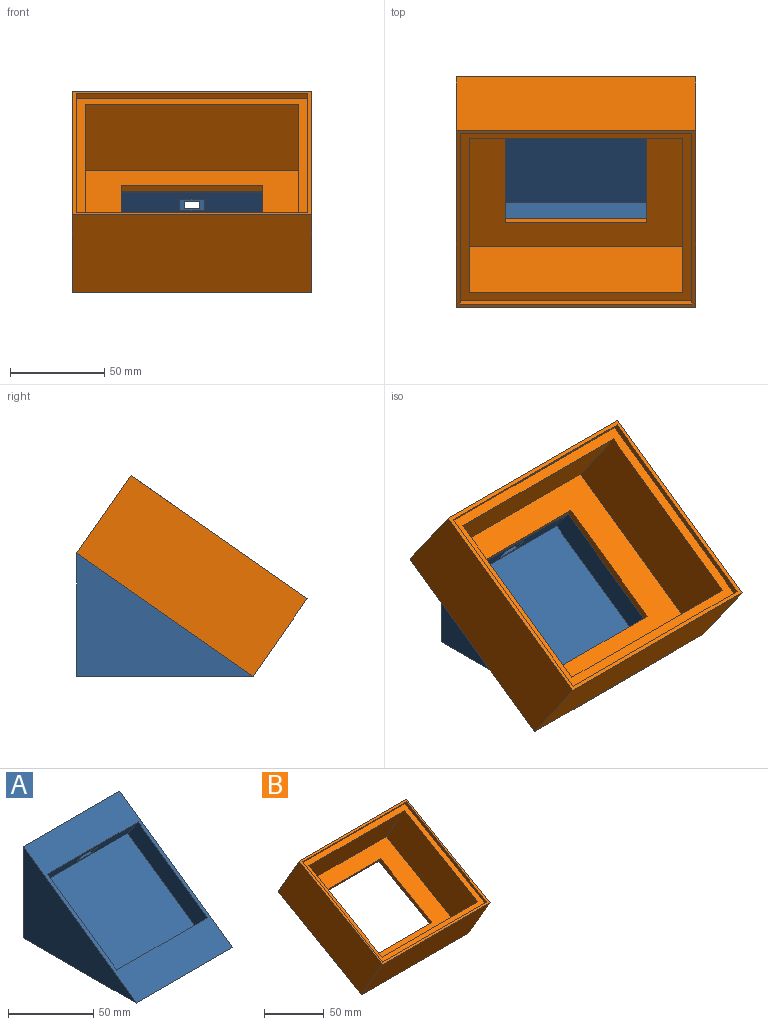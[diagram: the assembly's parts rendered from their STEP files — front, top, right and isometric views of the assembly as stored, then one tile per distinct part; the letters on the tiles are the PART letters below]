
ASSEMBLY  parts=2 mates=1
PART A: 33 faces, bbox 80x93.5x65.5 mm
  f0: plane 80x65.47mm, normal (0,1,0), area 5204.6mm2, adj f2,f3,f4,f5,f14,f15,f16,f17
  f1: plane 75x12.29mm, normal (0,-0.82,-0.57), area 1025.8mm2, adj f2,f6,f8,f9,f10,f11,f12,f13
  f2: plane 93.5x80mm, normal (0,-0.57,0.82), area 3881.4mm2, adj f0,f1,f3,f4,f5,f6,f7,f8
  f3: plane 93.5x80mm, normal (0,0,-1), area 1415.7mm2, adj f0,f2,f4,f5,f19,f20,f21,f22
  f4: plane 93.5x65.47mm, normal (1,0,0), area 3060.7mm2, adj f0,f2,f3
  f5: plane 93.5x65.47mm, normal (-1,0,0), area 3060.7mm2, adj f0,f2,f3
  f6: plane 65.94x52.44mm, normal (1,0,0), area 1050mm2, adj f1,f2,f7,f9
  f7: plane 75x12.29mm, normal (0,0.82,0.57), area 1125mm2, adj f2,f6,f8,f9
  f8: plane 65.94x52.44mm, normal (-1,0,0), area 1050mm2, adj f1,f2,f7,f9
  f9: plane 75x57.34mm, normal (0,-0.57,0.82), area 5250mm2, adj f1,f6,f7,f8
  f10: plane 13x7.52mm, normal (0,0,1), area 97.8mm2, adj f1,f11,f13,f18
  f11: plane 11.9x6.25mm, normal (1,0,0), area 60.7mm2, adj f1,f10,f12,f18
  f12: plane 13x11.9mm, normal (0,0,-1), area 154.7mm2, adj f1,f11,f13,f18
  f13: plane 11.9x6.25mm, normal (-1,0,0), area 60.7mm2, adj f1,f10,f12,f18
  f14: plane 4x3mm, normal (1,0,0), area 12mm2, adj f0,f15,f17,f18
  f15: plane 8.25x3mm, normal (0,0,1), area 24.7mm2, adj f0,f14,f16,f18
  f16: plane 4x3mm, normal (-1,0,0), area 12mm2, adj f0,f15,f17,f18
  f17: plane 8.25x3mm, normal (0,0,-1), area 24.7mm2, adj f0,f14,f16,f18
  f18: plane 13x6.25mm, normal (0,-1,0), area 48.3mm2, adj f10,f11,f12,f13,f14,f15,f16,f17
  f19: plane 75x13.67mm, normal (0,0.57,-0.82), area 1251.3mm2, adj f3,f20,f21,f22
  f20: plane 20.37x9.57mm, normal (-1,0,0), area 97.5mm2, adj f3,f19,f22
  f21: plane 20.37x9.57mm, normal (1,0,0), area 97.5mm2, adj f3,f19,f22
  f22: plane 75x9.57mm, normal (0,-0.82,-0.57), area 876.2mm2, adj f3,f19,f20,f21
  f23: plane 75x57.56mm, normal (0,0.57,-0.82), area 5269.7mm2, adj f3,f24,f27,f28
  f24: plane 75x12.29mm, normal (0,0.82,0.57), area 877.8mm2, adj f23,f26,f27,f28,f29,f30,f31,f32
  f25: plane 75x60.67mm, normal (0,-1,0), area 4347.5mm2, adj f3,f26,f27,f28,f29,f30,f31,f32
  f26: plane 75x11.54mm, normal (0,0.57,-0.82), area 1056.4mm2, adj f24,f25,f27,f28
  f27: plane 60.67x60.49mm, normal (1,0,0), area 1413.5mm2, adj f3,f23,f24,f25,f26
  f28: plane 60.67x60.49mm, normal (-1,0,0), area 1413.5mm2, adj f3,f23,f24,f25,f26
  f29: plane 18x3.22mm, normal (0,0,-1), area 57.9mm2, adj f24,f25,f30,f32
  f30: plane 11.25x11.1mm, normal (1,0,0), area 80.5mm2, adj f24,f25,f29,f31
  f31: plane 18x11.1mm, normal (0,0,1), area 199.7mm2, adj f24,f25,f30,f32
  f32: plane 11.25x11.1mm, normal (-1,0,0), area 80.5mm2, adj f24,f25,f29,f31
PART B: 20 faces, bbox 127x123.7x100.3 mm
  f0: plane 127x98.73mm, normal (0,0.5,-0.87), area 9228mm2, adj f3,f4,f5,f6,f16,f17,f18,f19
  f1: plane 113x86.6mm, normal (0,-0.5,0.87), area 6050mm2, adj f12,f13,f14,f15,f16,f17,f18,f19
  f2: plane 127x98.73mm, normal (0,-0.5,0.87), area 948mm2, adj f3,f4,f5,f6,f7,f8,f9,f10
  f3: plane 127x43.3mm, normal (0,-0.87,-0.5), area 6350mm2, adj f0,f2,f4,f6
  f4: plane 123.73x100.3mm, normal (1,0,0), area 5700mm2, adj f0,f2,f3,f5
  f5: plane 127x43.3mm, normal (0,0.87,0.5), area 6350mm2, adj f0,f2,f4,f6
  f6: plane 123.73x100.3mm, normal (-1,0,0), area 5700mm2, adj f0,f2,f3,f5
  f7: plane 96.86x57.77mm, normal (1,0,0), area 352mm2, adj f2,f8,f10,f11
  f8: plane 123x2.77mm, normal (0,0.87,0.5), area 393.6mm2, adj f2,f7,f9,f11
  f9: plane 96.86x57.77mm, normal (-1,0,0), area 352mm2, adj f2,f8,f10,f11
  f10: plane 123x2.77mm, normal (0,-0.87,-0.5), area 393.6mm2, adj f2,f7,f9,f11
  f11: plane 123x95.26mm, normal (0,-0.5,0.87), area 2230mm2, adj f7,f8,f9,f10,f12,f13,f14,f15
  f12: plane 108x87.07mm, normal (1,0,0), area 4280mm2, adj f1,f11,f13,f15
  f13: plane 113x37.07mm, normal (0,0.87,0.5), area 4836.4mm2, adj f1,f11,f12,f14
  f14: plane 108x87.07mm, normal (-1,0,0), area 4280mm2, adj f1,f11,f13,f15
  f15: plane 113x37.07mm, normal (0,-0.87,-0.5), area 4836.4mm2, adj f1,f11,f12,f14
  f16: plane 75x3.46mm, normal (0,0.87,0.5), area 300mm2, adj f0,f1,f17,f19
  f17: plane 62.62x38.46mm, normal (1,0,0), area 280mm2, adj f0,f1,f16,f18
  f18: plane 75x3.46mm, normal (0,-0.87,-0.5), area 300mm2, adj f0,f1,f17,f19
  f19: plane 62.62x38.46mm, normal (-1,0,0), area 280mm2, adj f0,f1,f16,f18
PLACE A at identity fixed
PLACE B rot(axis=(1,0,0),5deg) t=(0,-4.21,5.05)mm
MATE fastened A.f2 <-> B.f0  axis (0,-0.57,0.82) through (0,32.39,65.47)mm
